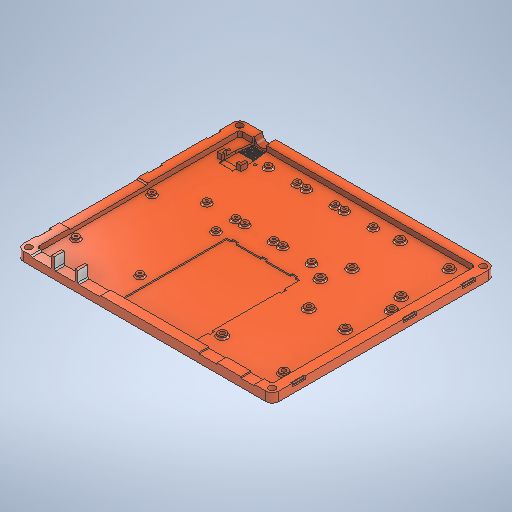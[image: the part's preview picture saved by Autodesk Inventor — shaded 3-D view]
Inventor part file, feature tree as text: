
AUTODESK INVENTOR PART (.ipt)
format: ipt  version: 2025.2 (Build 292293000, 293)  size: 987,136 bytes
history: native  units: mm
features: extrude x18, sketch x11, plane x6, fillet x4, mirror x3, chamfer x2, hole x1
ambient origin geometry x8: Origin, YZ Plane, XZ Plane, XY Plane, X Axis, Y Axis, Z Axis, Center Point
bodies: Solid1 (feature_tree)
feature tree (45):
  sketch  "Sketch1"  dims[d10=1.8mm d11=3.5mm]
  extrude  "Base"  Depth=3.5mm
  extrude  "Wall"  Depth=4.0mm TaperAngle=0.0deg
  extrude  "Breadboard Slot"  Depth=5.0mm
  extrude  "Electronic Mounting Holes"  Depth=7.5mm
  extrude  "Deeper Mounting Holes"  Depth=1.5mm
  chamfer  "Chamfer2"  Distance=50.8mm
  fillet  "Fillet1"  Radius=66.04mm
  fillet  "Fillet3"  Radius=17.78mm
  sketch  "Sketch2"  dims[d37=2.0mm d38=0.0mm d39=5.0mm]
  extrude  "Board ports"  Depth=0.5mm
  chamfer  "Chamfer3"  Distance=13.97mm
  extrude  "Extrusion18"  Depth=85.0mm
  fillet  "Fillet5"  Radius=58.0mm
  sketch  "Sketch3"  dims[d62=3.1mm d63=1.5mm]
  plane  "Work Plane6"
  plane  "Work Plane7"
  plane  "Work Plane8"
  extrude  "Extrusion6"  Depth=1.5mm
  extrude  "Extrusion16"  Depth=3.5mm
  extrude  "Extrusion17"  Depth=3.5mm
  fillet  "Fillet4"  Radius=3.5mm
  plane  "Work Plane3"
  mirror  "Mirror2"
  sketch  "Sketch4"  dims[d79=7.5mm]
  extrude  "Extrusion7"  Depth=56.0mm
  hole  "Hole1"  [1 undecoded]
  mirror  "Mirror3"
  plane  "Work Plane9"
  mirror  "Mirror5"
  sketch  "Sketch6"  dims[d82=2.54mm]
  extrude  "DC terminal slot"  Depth=0.5mm
  extrude  "DC terminal ribs"  Depth=16.0mm
  extrude  "DC terminal output"  Depth=16.0mm
  extrude  "DC terminal port"  Depth=17.5mm
  extrude  "Extrusion13"  Depth=1.0mm TaperAngle=0.0deg
  extrude  "DC Jack Test Fit"  Depth=13.64mm
  extrude  "Extrusion14"  Depth=1.0mm
  sketch  "Sketch Rectangular Pattern1"  dims[d19=3.0mm d20=0.0mm d21=4.0mm d22=0.0mm]
  sketch  "Sketch Rectangular Pattern2"  dims[d49=53.34mm d59=7.5mm]
  sketch  "Sketch Rectangular Pattern3"  dims[d73=7.5mm]
  plane  "Work Plane4"
  sketch  "Sketch7"  dims[d83=15.24mm]
  sketch  "Sketch8"  dims[d84=90.17mm]
  sketch  "Sketch9"  dims[d85=96.52mm d86=50.8mm d87=66.04mm d88=17.78mm d89=45.72mm d90=13.97mm d91=85.0mm d92=58.0mm d95=1.5mm d96=3.5mm d97=3.5mm d98=3.5mm d99=56.0mm d102=7.5mm d103=65.0mm d104=16.0mm d107=16.0mm d109=17.5mm d110=1.0mm d111=0.0mm d113=13.64mm d114=1.0mm d115=19.0mm d116=37.0mm d117=8.5mm d118=40.5mm d119=10.33mm d121=54.75mm d122=81.68mm d123=1.0mm d124=43.0mm d131=51.0mm d134=101.6mm d135=26.0mm d141=49.0mm d142=30.0mm d144=29.0mm d145=10.0mm d147=10.0mm d149=0.5mm d150=4.0mm d151=1.5mm d152=30.0mm d154=22.7mm d155=10.0mm d157=10.0mm d160=11.9mm d163=20.0mm d165=54.53mm d166=10.0mm d168=10.0mm d170=1.0mm d171=0.0mm d172=30.0mm d173=8.0mm d174=2.0mm d176=2.8mm d178=5.0mm d179=3.32mm d180=2.871mm d181=40.244mm d182=40.057mm d190=10.0mm d191=0.0mm d201=1.0mm d205=5.7mm d206=4.5mm d207=4.5mm d208=1.0mm d209=0.0mm d210=2.5mm d211=1.0mm d215=3.0mm d216=6.0mm d217=5.0mm d218=3.2mm d219=90.0deg d220=8.0mm d221=20.594885mm d222=45.0deg d223=10.5mm d224=14.0mm d226=1.6mm d227=0.8mm d228=1.2mm d229=0.8mm d230=1.2mm d231=0.8mm d232=1.2mm d235=0.8mm d240=6.0mm d241=0.8mm d242=1.2mm d243=6.0mm d244=0.0mm d245=0.5mm d246=0.0mm d247=1.0mm d248=0.0mm d249=6.0mm d250=10.0mm d251=0.0mm d252=0.0mm d253=10.5mm d254=4.5mm d255=1.2mm d256=25.0mm d257=35.0mm d258=9.95mm d259=0.0mm d260=0.8mm d261=13.0mm d262=9.5mm d263=4.5mm d265=2.0mm d266=2.0mm d267=3.0mm d268=1.5mm d269=1.0mm d270=0.0mm d272=20.0mm d273=2.0mm d274=8.0mm d275=10.0mm d276=0.0mm d278=1.5mm d279=2.0mm d280=2.0mm d281=1.8mm d282=4.8mm d283=1.0mm d284=2.0mm d285=45.0deg d286=2.0mm d287=0.0mm d288=2.0mm d289=-20.0mm d290=-105.0mm d291=10.0mm d292=0.0mm d293=-150.0mm d294=10.0mm d295=0.0mm d296=1.0mm d297=15.0mm d298=155.0mm d299=4.5mm d300=25.0mm d301=85.0mm d302=8.0mm d303=0.0mm d304=1.0mm d305=180.0mm d306=1.0mm d307=2.0mm d308=45.0deg d74=0.5mm d75=0.872665mm d76=0.5mm d77=0.872665mm d225=0.872665mm]
note: 1 required parameter value undecoded (feature->parameter linkage not recoverable at this tier; creation-order binding heuristic only, values carry confidence <= 0.55)
